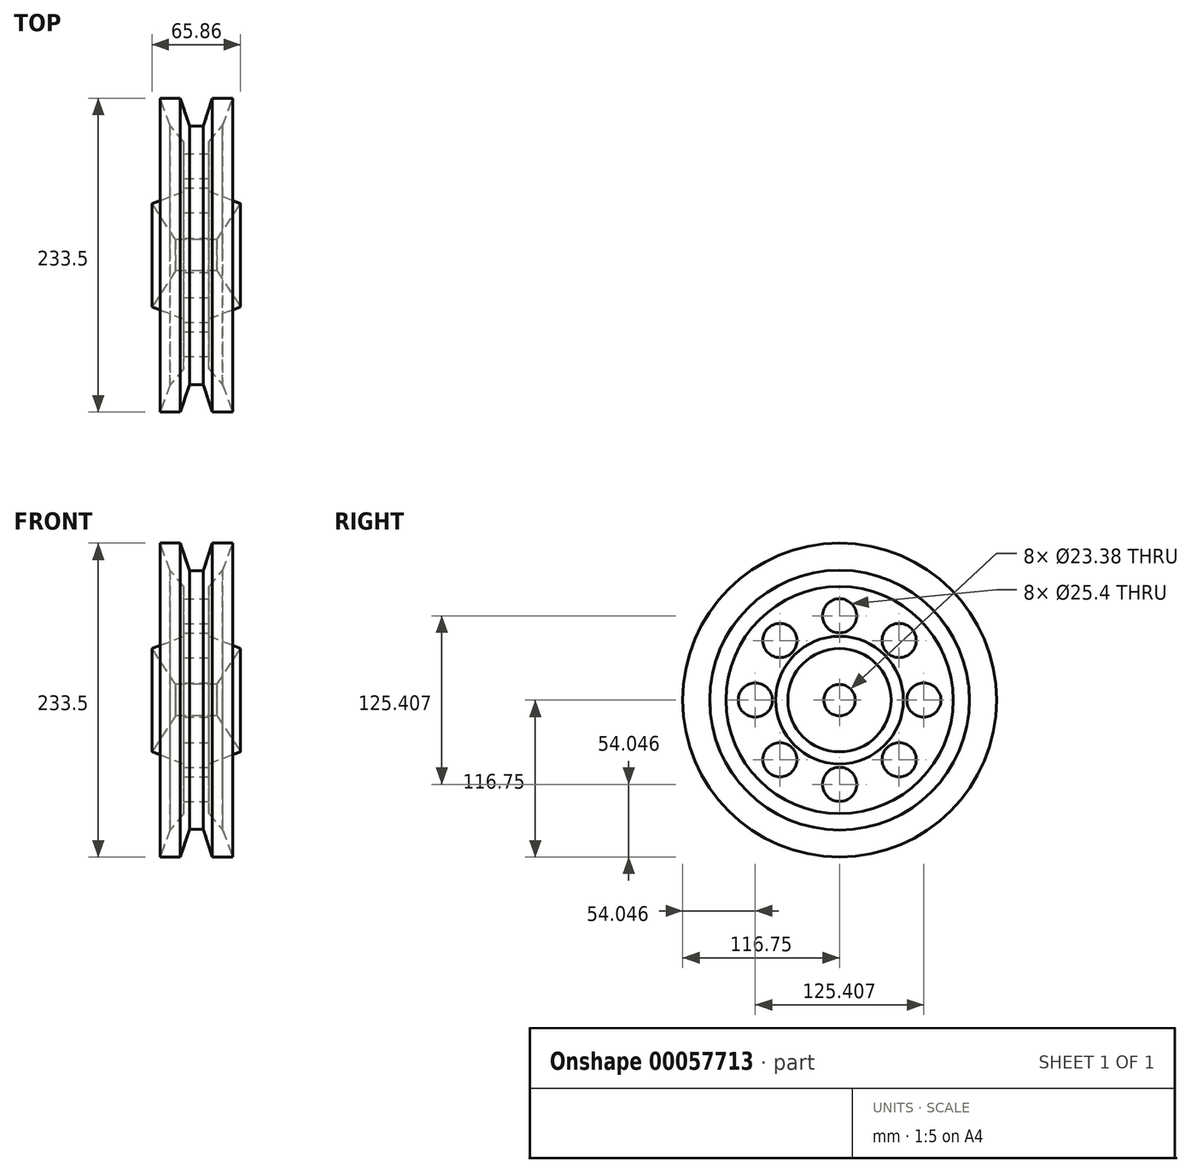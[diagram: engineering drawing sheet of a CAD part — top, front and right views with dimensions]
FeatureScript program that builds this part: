
annotation { "Feature Type Name" : "Feature", "Feature Type Description" : "" }
export const myFeature = defineFeature(function(context is Context, id is Id, definition is map)
    precondition{}
    {
        {
            var Q0;
            Q0=qCreatedBy(makeId("Top.planeOp"),FACE);
            var sketch = newSketch(context, id + "F0", { "sketchPlane" : qUnion([Q0])});
            skLineSegment(sketch, "E0", {"start": v(0, 11.69) * mm, "end": v(15.45, 11.69) * mm});
            skLineSegment(sketch, "E1", {"start": v(15.45, 11.69) * mm, "end": v(32.93, 38.44) * mm});
            skLineSegment(sketch, "E2", {"start": v(32.93, 38.44) * mm, "end": v(9.38, 47.45) * mm});
            skLineSegment(sketch, "E3", {"start": v(9.38, 47.45) * mm, "end": v(9.38, 84.49) * mm});
            skLineSegment(sketch, "E4", {"start": v(9.38, 84.49) * mm, "end": v(19.6, 96.62) * mm});
            skLineSegment(sketch, "E5", {"start": v(19.6, 96.62) * mm, "end": v(27.08, 116.75) * mm});
            skLineSegment(sketch, "E6", {"start": v(27.08, 116.75) * mm, "end": v(11.95, 116.75) * mm});
            skLineSegment(sketch, "E7", {"start": v(11.95, 116.75) * mm, "end": v(5.13, 96.2) * mm});
            skLineSegment(sketch, "E8", {"start": v(5.13, 96.2) * mm, "end": v(0, 96.2) * mm});
            skLineSegment(sketch, "E9", {"start": v(0, 96.2) * mm, "end": v(0, 11.69) * mm});
            skLineSegment(sketch, "E10", {"start": v(0, 0) * mm, "end": v(41.37, 0) * mm});
            skSolve(sketch);
        }
        {
            var Q0;
            Q0=makeQuery(id+"F0.imprint","IMPRINT",FACE,{"disambiguationData":[TD([[makeQuery(id+"F0.imprint","IMPRINT",EDGE,{"derivedFrom":sQuery(id+"F0.wireOp",EDGE,"E0")}),1.0]])]});
            var Q1;
            Q1=sQuery(id+"F0.wireOp",EDGE,"E10");
            revolve(context, id + "F1", {"entities" : qUnion([Q0]), "axis" : qUnion([Q1]), "revolveType" : RevolveType.FULL});
        }
        {
            var Q0;
            Q0=makeQuery(id+"F1.opRevolve","SWEPT_BODY",BODY,{"disambiguationData":[OSD([sQuery(id+"F0.wireOp",EDGE,"E0"),sQuery(id+"F0.wireOp",EDGE,"E1"),sQuery(id+"F0.wireOp",EDGE,"E2"),sQuery(id+"F0.wireOp",EDGE,"E3"),sQuery(id+"F0.wireOp",EDGE,"E4"),sQuery(id+"F0.wireOp",EDGE,"E5"),sQuery(id+"F0.wireOp",EDGE,"E6"),sQuery(id+"F0.wireOp",EDGE,"E7"),sQuery(id+"F0.wireOp",EDGE,"E8"),sQuery(id+"F0.wireOp",EDGE,"E9")])]});
            var Q1;
            Q1=qCreatedBy(makeId("Right.planeOp"),FACE);
            mirror(context, id + "F2", {"operationType" : NewBodyOperationType.ADD, "entities" : qUnion([Q0]), "mirrorPlane" : qUnion([Q1])});
        }
        {
            var Q0;
            Q0=makeQuery(id+"F1.opRevolve","SWEPT_FACE",FACE,{"disambiguationData":[OSD([sQuery(id+"F0.wireOp",EDGE,"E3")])]});
            var sketch = newSketch(context, id + "F3", { "sketchPlane" : qUnion([Q0])});
            skCircle(sketch, "E11", {"center": v(62.7, 0) * mm, "radius": 12.37 * mm});
            skSolve(sketch);
        }
        {
            var Q0;
            Q0=sQuery(id+"F3.wireOp",VERTEX,"E11.center");
            var Q1;
            Q1=makeQuery(id+"F1.opRevolve","SWEPT_BODY",BODY,{"disambiguationData":[OSD([sQuery(id+"F0.wireOp",EDGE,"E0"),sQuery(id+"F0.wireOp",EDGE,"E1"),sQuery(id+"F0.wireOp",EDGE,"E2"),sQuery(id+"F0.wireOp",EDGE,"E3"),sQuery(id+"F0.wireOp",EDGE,"E4"),sQuery(id+"F0.wireOp",EDGE,"E5"),sQuery(id+"F0.wireOp",EDGE,"E6"),sQuery(id+"F0.wireOp",EDGE,"E7"),sQuery(id+"F0.wireOp",EDGE,"E8"),sQuery(id+"F0.wireOp",EDGE,"E9")])]});
            hole(context, id + "F4", {"style" : HoleStyle.SIMPLE, "holeDiameter" : 25.4 * mm, "endStyle" : HoleEndStyle.THROUGH, "locations" : qUnion([Q0]), "scope" : qUnion([Q1])});
        }
        {
            var Q0;
            Q0=makeQuery(id+"F1.opRevolve","SWEPT_BODY",BODY,{"disambiguationData":[OSD([sQuery(id+"F0.wireOp",EDGE,"E0"),sQuery(id+"F0.wireOp",EDGE,"E1"),sQuery(id+"F0.wireOp",EDGE,"E2"),sQuery(id+"F0.wireOp",EDGE,"E3"),sQuery(id+"F0.wireOp",EDGE,"E4"),sQuery(id+"F0.wireOp",EDGE,"E5"),sQuery(id+"F0.wireOp",EDGE,"E6"),sQuery(id+"F0.wireOp",EDGE,"E7"),sQuery(id+"F0.wireOp",EDGE,"E8"),sQuery(id+"F0.wireOp",EDGE,"E9")])]});
            var Q1;
            Q1=sQuery(id+"F0.wireOp",EDGE,"E10");
            circularPattern(context, id + "F5", {"entities" : qUnion([Q0]), "axis" : qUnion([Q1]), "angle" : 360 * degree, "instanceCount" : 8, "equalSpace" : true});
        }
    });
